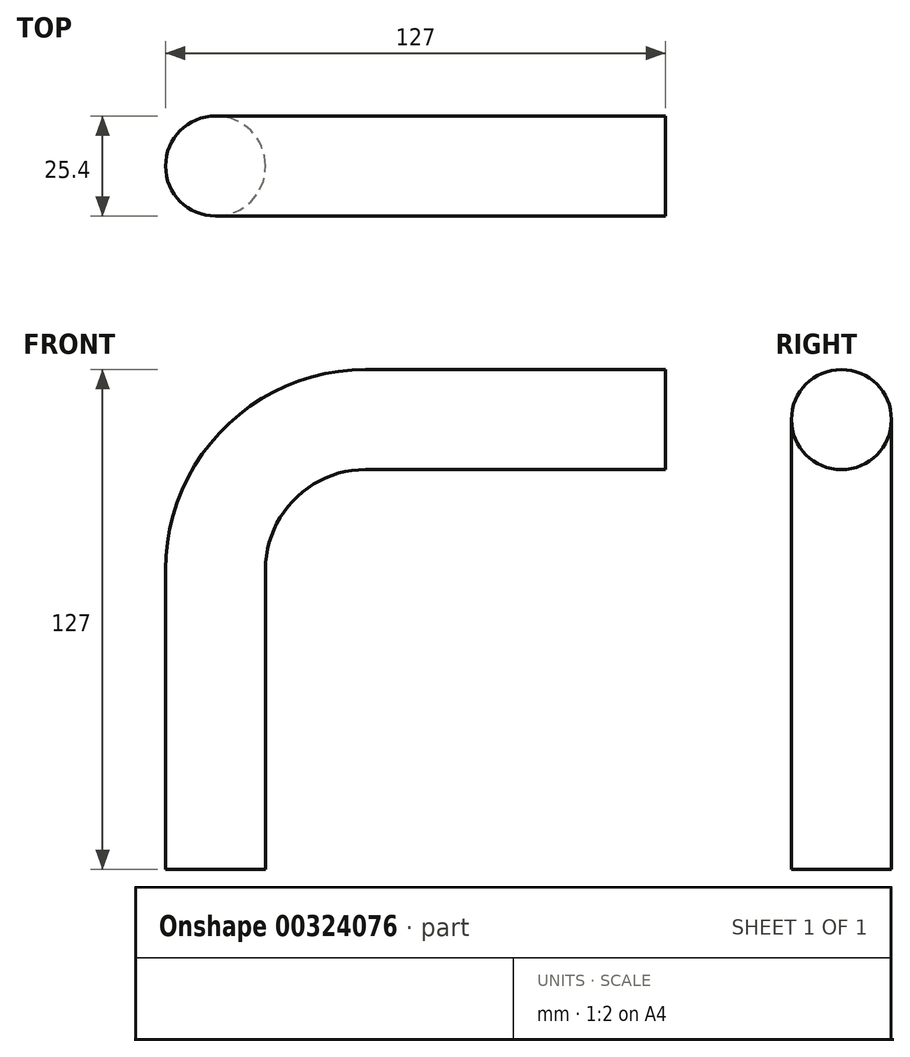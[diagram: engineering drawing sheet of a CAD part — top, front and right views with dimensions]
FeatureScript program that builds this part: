
annotation { "Feature Type Name" : "Feature", "Feature Type Description" : "" }
export const myFeature = defineFeature(function(context is Context, id is Id, definition is map)
    precondition{}
    {
        {
            var Q0;
            Q0=qCreatedBy(makeId("Top.planeOp"),FACE);
            var sketch = newSketch(context, id + "F0", { "sketchPlane" : qUnion([Q0])});
            skCircle(sketch, "E0", {"center": v(0, 0) * mm, "radius": 12.7 * mm});
            skSolve(sketch);
        }
        {
            var Q0;
            Q0=qCreatedBy(makeId("Front.planeOp"),FACE);
            var sketch = newSketch(context, id + "F1", { "sketchPlane" : qUnion([Q0])});
            skLineSegment(sketch, "E1", {"start": v(0, 0) * mm, "end": v(0, 76.2) * mm});
            skArc(sketch, "E2", {"start": v(38.1, 114.3) * mm, "mid": v(11.16, 103.14) * mm, "end": v(0, 76.2) * mm});
            skLineSegment(sketch, "E3", {"start": v(38.1, 114.3) * mm, "end": v(114.3, 114.3) * mm});
            skSolve(sketch);
        }
        {
            var Q0;
            Q0=makeQuery(id+"F0.imprint","IMPRINT",FACE,{"disambiguationData":[TD([[makeQuery(id+"F0.imprint","IMPRINT",EDGE,{"derivedFrom":sQuery(id+"F0.wireOp",EDGE,"E0")}),1.0]])]});
            var Q1;
            Q1=sQuery(id+"F1.wireOp",EDGE,"E2");
            var Q2;
            Q2=sQuery(id+"F1.wireOp",EDGE,"E1");
            var Q3;
            Q3=sQuery(id+"F1.wireOp",EDGE,"E3");
            sweep(context, id + "F2", {"profiles" : qUnion([Q0]), "path" : qUnion([Q1, Q2, Q3])});
        }
        {
            var Q0;
            Q0=qCreatedBy(makeId("Top.planeOp"),FACE);
            cPlane(context, id + "F3", {"entities" : qUnion([Q0]), "cplaneType" : CPlaneType.OFFSET, "offset" : 139.7 * mm, "width" : 152.4 * mm, "height" : 152.4 * mm});
        }
    });
